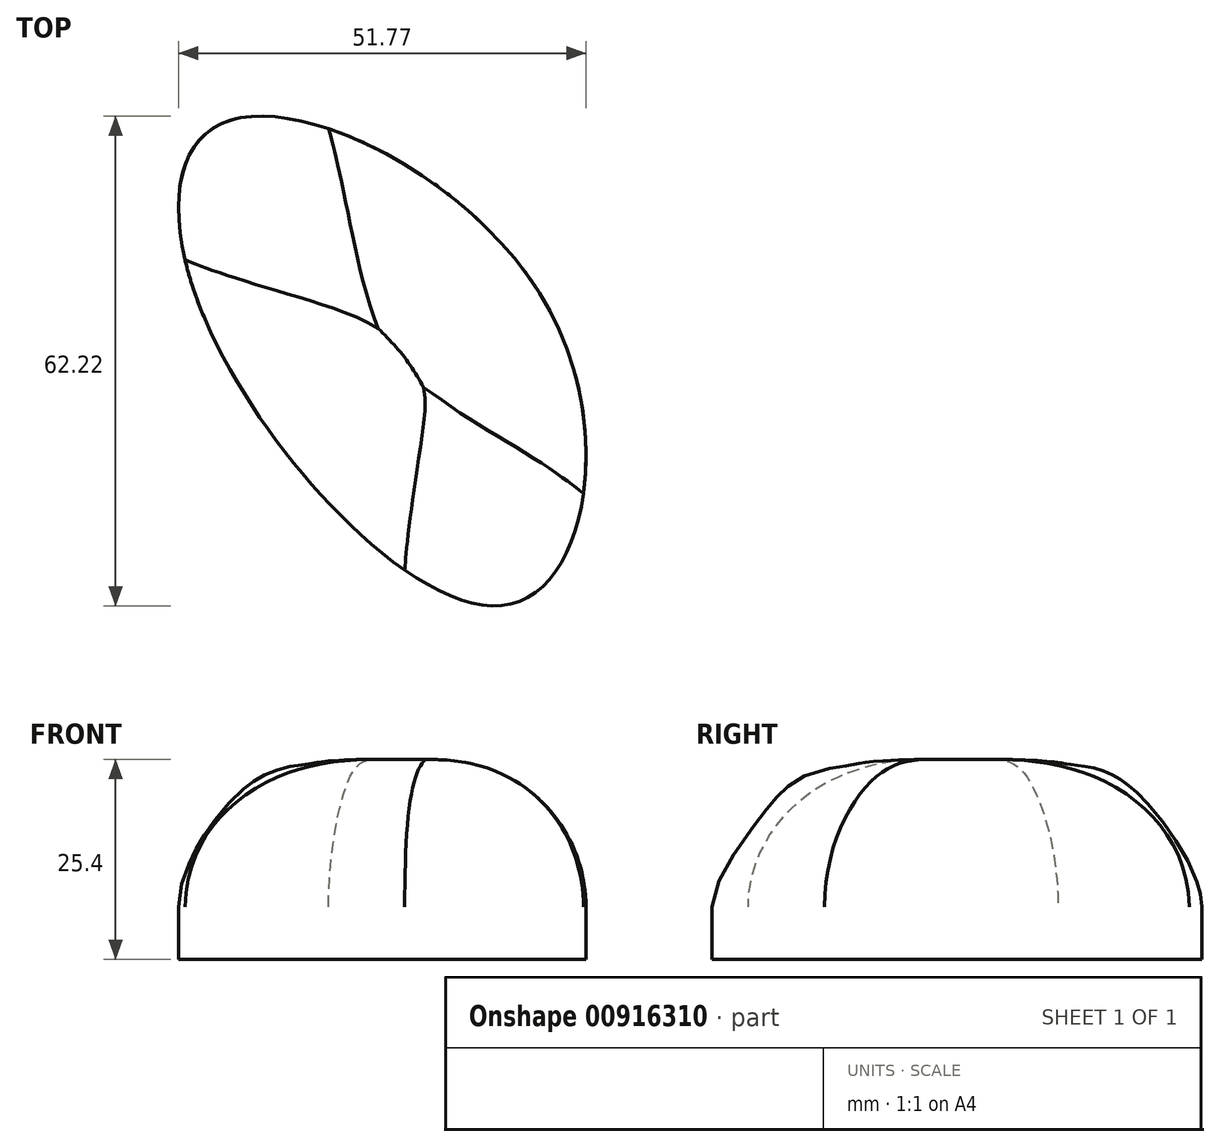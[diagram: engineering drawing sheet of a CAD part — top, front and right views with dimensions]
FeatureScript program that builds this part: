
annotation { "Feature Type Name" : "Feature", "Feature Type Description" : "" }
export const myFeature = defineFeature(function(context is Context, id is Id, definition is map)
    precondition{}
    {
        {
            var Q0;
            Q0=qCreatedBy(makeId("Top.planeOp"),FACE);
            var sketch = newSketch(context, id + "F0", { "sketchPlane" : qUnion([Q0])});
            skFitSpline(sketch, "E0", {"points": [v(0, 0) * mm, v(39.01, -36.17) * mm, v(44.38, 0) * mm, v(2.91, 25.16) * mm, v(0, 0) * mm]});
            skSolve(sketch);
        }
        {
            var Q0;
            Q0=makeQuery(id+"F0.imprint","IMPRINT",FACE,{"disambiguationData":[TD([[makeQuery(id+"F0.imprint","IMPRINT",EDGE,{"derivedFrom":sQuery(id+"F0.wireOp",EDGE,"E0")}),1.0]])]});
            extrude(context, id + "F1", {"entities" : qUnion([Q0]), "depth" : 25.4 * mm, "offsetDistance" : 25.4 * mm});
        }
        {
            var Q0;
            Q0=makeQuery(id+"F1.opExtrude","CAP_EDGE",EDGE,{"disambiguationData":[OSD([sQuery(id+"F0.wireOp",EDGE,"E0")])],"isStart":false});
            fillet(context, id + "F2", {"entities" : qUnion([Q0]), "radius" : 18.76 * mm, "tangentPropagation" : true, "allowEdgeOverflow" : false});
        }
    });
